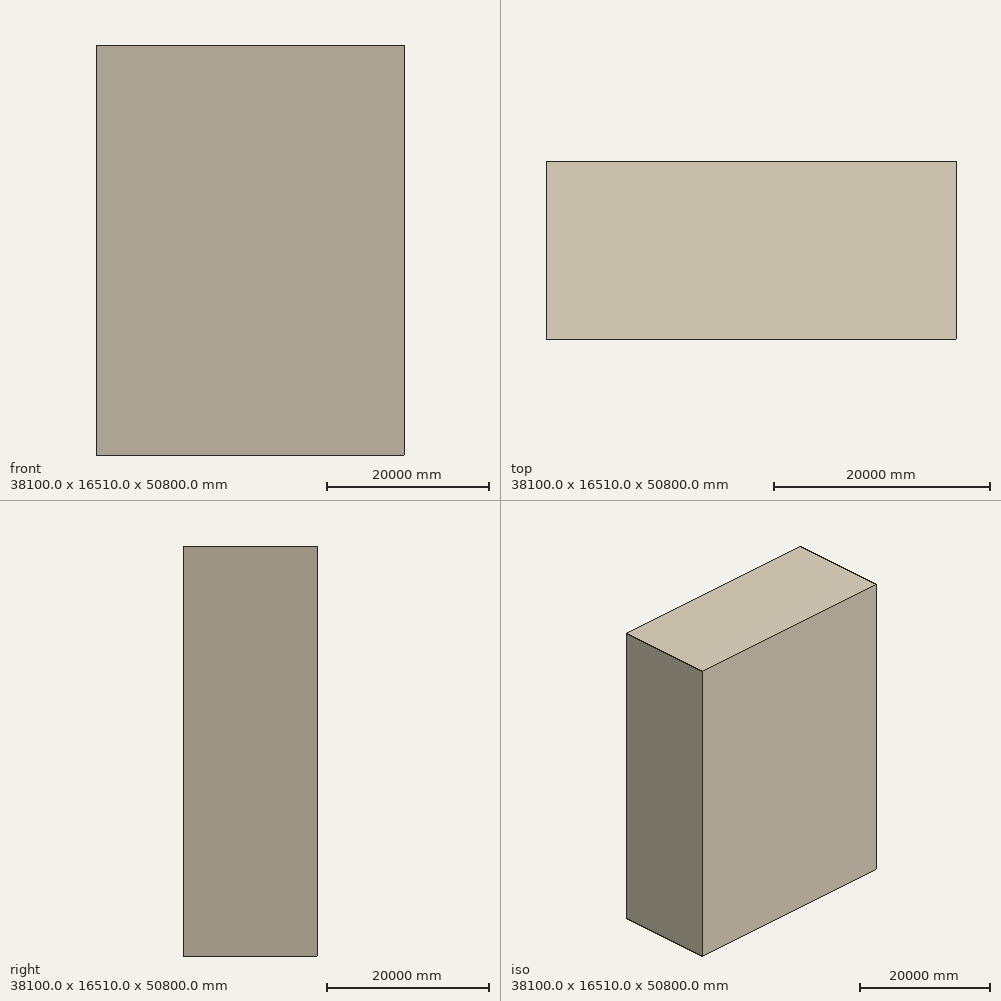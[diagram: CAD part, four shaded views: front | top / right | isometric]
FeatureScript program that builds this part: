
annotation { "Feature Type Name" : "Feature", "Feature Type Description" : "" }
export const myFeature = defineFeature(function(context is Context, id is Id, definition is map)
    precondition{}
    {
        {
            var Q0;
            Q0=qCreatedBy(makeId("Front.planeOp"),FACE);
            var sketch = newSketch(context, id + "F0", { "sketchPlane" : qUnion([Q0])});
            skLineSegment(sketch, "E0.bottom", {"start": v(-33043.86, 25401.04) * mm, "end": v(5056.14, 25401.04) * mm});
            skLineSegment(sketch, "E0.top", {"start": v(-33043.86, -25398.96) * mm, "end": v(5056.14, -25398.96) * mm});
            skLineSegment(sketch, "E0.left", {"start": v(-33043.86, 25401.04) * mm, "end": v(-33043.86, -25398.96) * mm});
            skLineSegment(sketch, "E0.right", {"start": v(5056.14, 25401.04) * mm, "end": v(5056.14, -25398.96) * mm});
            skSolve(sketch);
        }
        {
            var Q0;
            Q0=makeQuery(id+"F0.imprint","IMPRINT",FACE,{"disambiguationData":[TD([[makeQuery(id+"F0.imprint","IMPRINT",EDGE,{"derivedFrom":sQuery(id+"F0.wireOp",EDGE,"E0.bottom")}),-1.0]])]});
            extrude(context, id + "F1", {"entities" : qUnion([Q0]), "depth" : 16510 * mm, "offsetDistance" : 25.4 * mm});
        }
    });
